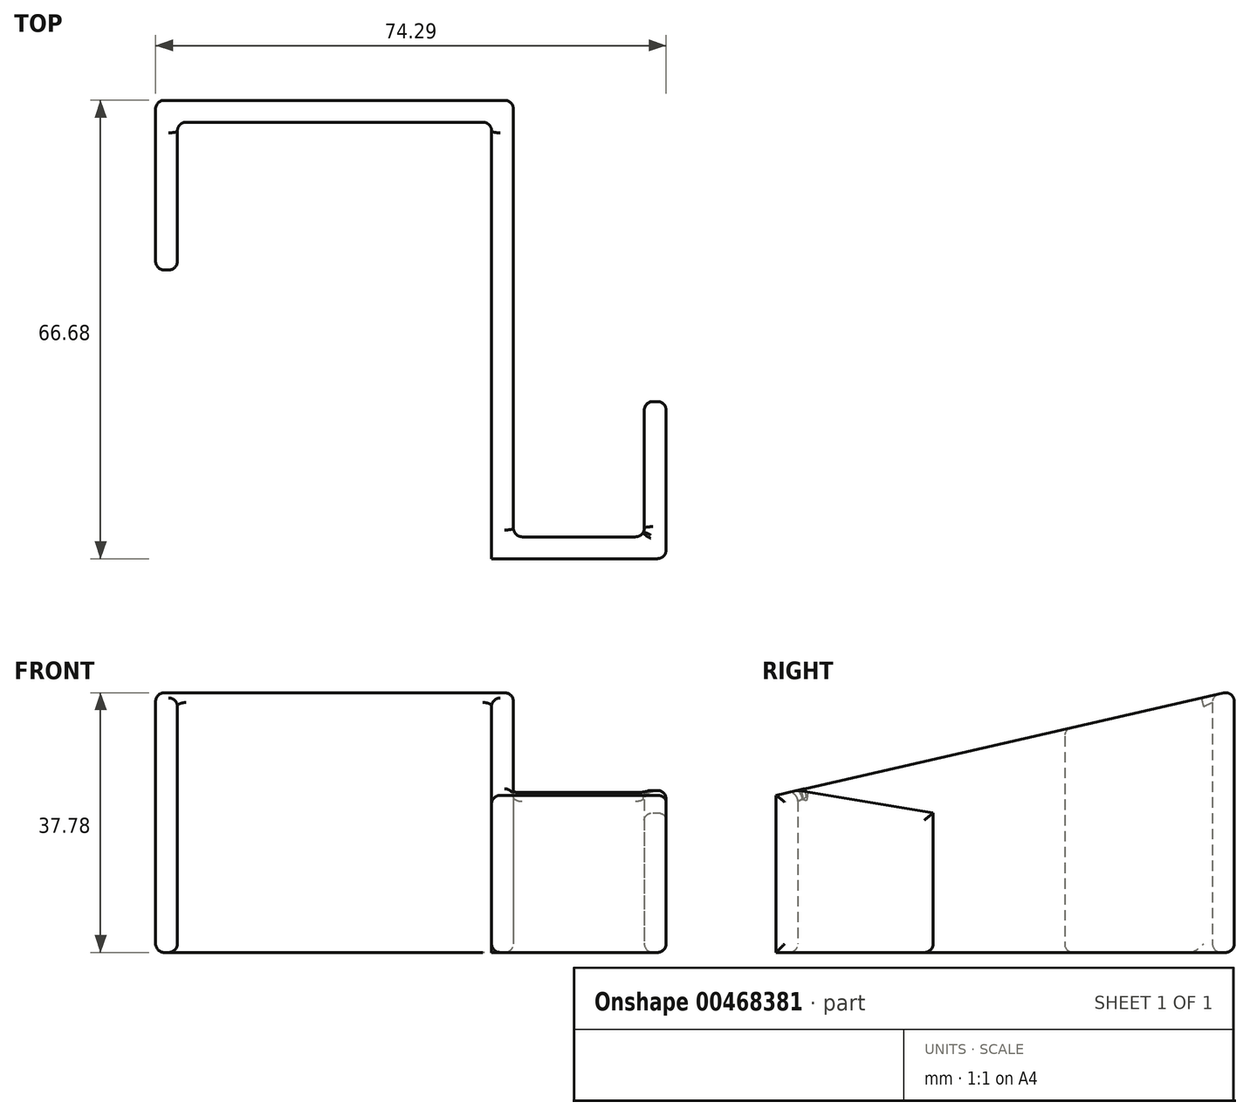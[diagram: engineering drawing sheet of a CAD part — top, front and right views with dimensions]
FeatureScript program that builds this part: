
annotation { "Feature Type Name" : "Feature", "Feature Type Description" : "" }
export const myFeature = defineFeature(function(context is Context, id is Id, definition is map)
    precondition{}
    {
        {
            var Q0;
            Q0=qCreatedBy(makeId("Top.planeOp"),FACE);
            var sketch = newSketch(context, id + "F0", { "sketchPlane" : qUnion([Q0])});
            skLineSegment(sketch, "E0", {"start": v(-23.13, 0) * mm, "end": v(-23.13, 21.5) * mm});
            skLineSegment(sketch, "E1", {"start": v(-23.13, 21.5) * mm, "end": v(22.6, 21.5) * mm});
            skLineSegment(sketch, "E2", {"start": v(22.6, 21.5) * mm, "end": v(22.6, -42) * mm});
            skLineSegment(sketch, "E3", {"start": v(22.6, -42) * mm, "end": v(48, -42) * mm});
            skLineSegment(sketch, "E4", {"start": v(48, -42) * mm, "end": v(48, -19.14) * mm});
            skLineSegment(sketch, "E5", {"start": v(48, -19.14) * mm, "end": v(44.82, -19.14) * mm});
            skLineSegment(sketch, "E6", {"start": v(44.82, -19.14) * mm, "end": v(44.82, -38.82) * mm});
            skLineSegment(sketch, "E7", {"start": v(44.82, -38.82) * mm, "end": v(25.77, -38.82) * mm});
            skLineSegment(sketch, "E8", {"start": v(25.77, -38.82) * mm, "end": v(25.77, 24.68) * mm});
            skLineSegment(sketch, "E9", {"start": v(25.77, 24.68) * mm, "end": v(-26.3, 24.68) * mm});
            skLineSegment(sketch, "E10", {"start": v(-26.3, 24.68) * mm, "end": v(-26.3, 0) * mm});
            skLineSegment(sketch, "E11", {"start": v(-26.3, 0) * mm, "end": v(-23.13, 0) * mm});
            skSolve(sketch);
        }
        {
            var Q0;
            Q0=makeQuery(id+"F0.imprint","IMPRINT",FACE,{"disambiguationData":[TD([[makeQuery(id+"F0.imprint","IMPRINT",EDGE,{"derivedFrom":sQuery(id+"F0.wireOp",EDGE,"E0")}),1.0]])]});
            extrude(context, id + "F1", {"entities" : qUnion([Q0]), "depth" : 38.1 * mm});
        }
        {
            var Q0;
            Q0=qCreatedBy(makeId("Right.planeOp"),FACE);
            var sketch = newSketch(context, id + "F2", { "sketchPlane" : qUnion([Q0])});
            skPoint(sketch, "E12.0", {"position": v(24.68, 38.1) * mm});
            skLineSegment(sketch, "E13", {"start": v(-42, 22.86) * mm, "end": v(24.68, 38.1) * mm});
            skLineSegment(sketch, "E14", {"start": v(-20.6, 65.52) * mm, "end": v(24.68, 38.1) * mm});
            skLineSegment(sketch, "E15", {"start": v(-20.6, 65.52) * mm, "end": v(-63.7, 38.1) * mm});
            skLineSegment(sketch, "E16", {"start": v(-63.7, 38.1) * mm, "end": v(-42, 22.86) * mm});
            skPoint(sketch, "E17.0.0.end.orphan", {"position": v(-19.14, 0) * mm});
            skPoint(sketch, "E17.0.1.end.orphan", {"position": v(-19.14, 38.1) * mm});
            skPoint(sketch, "E18.orphan", {"position": v(-42, 0) * mm});
            skPoint(sketch, "E19.0.start.orphan", {"position": v(-42, 38.1) * mm});
            skSolve(sketch);
        }
        {
            var Q0;
            Q0=makeQuery(id+"F2.imprint","IMPRINT",FACE,{"disambiguationData":[TD([[makeQuery(id+"F2.imprint","IMPRINT",EDGE,{"derivedFrom":sQuery(id+"F2.wireOp",EDGE,"E13")}),1.0]])]});
            extrude(context, id + "F3", {"entities" : qUnion([Q0]), "operationType" : NewBodyOperationType.REMOVE, "endBound" : BoundingType.SYMMETRIC, "oppositeDirection" : true, "depth" : 127 * mm});
        }
        {
            var Q0;
            Q0=makeQuery(id+"F1.opExtrude","SWEPT_FACE",FACE,{"disambiguationData":[OSD([sQuery(id+"F0.wireOp",EDGE,"E4")])]});
            var sketch = newSketch(context, id + "F4", { "sketchPlane" : qUnion([Q0])});
            skPoint(sketch, "E20.0.1.start.orphan", {"position": v(-19.14, 28.09) * mm});
            skLineSegment(sketch, "E21.0", {"start": v(-38.82, 23.59) * mm, "end": v(-19.14, 28.09) * mm});
            skLineSegment(sketch, "E22", {"start": v(-38.82, 23.59) * mm, "end": v(-19.14, 20.32) * mm});
            skPoint(sketch, "E23.orphan", {"position": v(-42, 0) * mm});
            skPoint(sketch, "E24.end.orphan", {"position": v(-19.14, 5.08) * mm});
            skPoint(sketch, "E20.0.3.end.orphan", {"position": v(-19.14, 0) * mm});
            skPoint(sketch, "E20.0.3.start.orphan", {"position": v(-38.82, 0) * mm});
            skLineSegment(sketch, "E25", {"start": v(-19.14, 20.32) * mm, "end": v(-19.14, 28.09) * mm});
            skSolve(sketch);
        }
        {
            var Q0;
            Q0=makeQuery(id+"F4.imprint","IMPRINT",FACE,{"disambiguationData":[TD([[makeQuery(id+"F4.imprint","IMPRINT",EDGE,{"derivedFrom":sQuery(id+"F4.wireOp",EDGE,"E21.0")}),1.0]])]});
            extrude(context, id + "F5", {"entities" : qUnion([Q0]), "operationType" : NewBodyOperationType.REMOVE, "oppositeDirection" : true, "depth" : 6.35 * mm});
        }
        {
            var Q0;
            Q0=makeQuery(id+"F1.opExtrude","SWEPT_FACE",FACE,{"disambiguationData":[OSD([sQuery(id+"F0.wireOp",EDGE,"E0")])]});
            var Q1;
            Q1=makeQuery(id+"F1.opExtrude","SWEPT_FACE",FACE,{"disambiguationData":[OSD([sQuery(id+"F0.wireOp",EDGE,"E8")])]});
            var Q2;
            Q2=makeQuery(id+"F1.opExtrude","SWEPT_FACE",FACE,{"disambiguationData":[OSD([sQuery(id+"F0.wireOp",EDGE,"E4")])]});
            var Q3;
            Q3=makeQuery(id+"F3.boolean.opBoolean","INTERSECT",EDGE,{"derivedFrom":[makeQuery(id+"F1.opExtrude","SWEPT_FACE",FACE,{"disambiguationData":[OSD([sQuery(id+"F0.wireOp",EDGE,"E7")])]}),makeQuery(id+"F3.opExtrude","SWEPT_FACE",FACE,{"disambiguationData":[OSD([sQuery(id+"F2.wireOp",EDGE,"E13")])]})]});
            var Q4;
            Q4=makeQuery(id+"F1.opExtrude","CAP_EDGE",EDGE,{"disambiguationData":[OSD([sQuery(id+"F0.wireOp",EDGE,"E1")])],"isStart":true});
            var Q5;
            Q5=makeQuery(id+"F1.opExtrude","SWEPT_EDGE",EDGE,{"disambiguationData":[OSD([sQuery(id+"F0.wireOp",EDGE,"E0"),sQuery(id+"F0.wireOp",EDGE,"E11")])]});
            var Q6;
            Q6=makeQuery(id+"F1.opExtrude","CAP_EDGE",EDGE,{"disambiguationData":[OSD([sQuery(id+"F0.wireOp",EDGE,"E7")])],"isStart":true});
            var Q7;
            Q7=makeQuery(id+"F1.opExtrude","SWEPT_EDGE",EDGE,{"disambiguationData":[OSD([sQuery(id+"F0.wireOp",EDGE,"E7"),sQuery(id+"F0.wireOp",EDGE,"E8")])]});
            var Q8;
            Q8=makeQuery(id+"F1.opExtrude","SWEPT_EDGE",EDGE,{"disambiguationData":[OSD([sQuery(id+"F0.wireOp",EDGE,"E0"),sQuery(id+"F0.wireOp",EDGE,"E1")])]});
            var Q9;
            Q9=makeQuery(id+"F1.opExtrude","SWEPT_EDGE",EDGE,{"disambiguationData":[OSD([sQuery(id+"F0.wireOp",EDGE,"E8"),sQuery(id+"F0.wireOp",EDGE,"E9")])]});
            var Q10;
            Q10=makeQuery(id+"F3.boolean.opBoolean","MERGE",EDGE,{"derivedFrom":[makeQuery(id+"F1.opExtrude","CAP_EDGE",EDGE,{"disambiguationData":[OSD([sQuery(id+"F0.wireOp",EDGE,"E9")])],"isStart":false}),makeQuery(id+"F3.opExtrude","SWEPT_EDGE",EDGE,{"disambiguationData":[OSD([sQuery(id+"F2.wireOp",EDGE,"E13"),sQuery(id+"F2.wireOp",EDGE,"E14")])]})]});
            var Q11;
            Q11=makeQuery(id+"F3.boolean.opBoolean","INTERSECT",EDGE,{"derivedFrom":[makeQuery(id+"F1.opExtrude","SWEPT_FACE",FACE,{"disambiguationData":[OSD([sQuery(id+"F0.wireOp",EDGE,"E1")])]}),makeQuery(id+"F3.opExtrude","SWEPT_FACE",FACE,{"disambiguationData":[OSD([sQuery(id+"F2.wireOp",EDGE,"E13")])]})]});
            var Q12;
            Q12=makeQuery(id+"F1.opExtrude","CAP_EDGE",EDGE,{"disambiguationData":[OSD([sQuery(id+"F0.wireOp",EDGE,"E0")])],"isStart":true});
            var Q13;
            Q13=makeQuery(id+"F1.opExtrude","SWEPT_EDGE",EDGE,{"disambiguationData":[OSD([sQuery(id+"F0.wireOp",EDGE,"E10"),sQuery(id+"F0.wireOp",EDGE,"E11")])]});
            var Q14;
            Q14=makeQuery(id+"F3.boolean.opBoolean","INTERSECT",EDGE,{"derivedFrom":[makeQuery(id+"F1.opExtrude","SWEPT_FACE",FACE,{"disambiguationData":[OSD([sQuery(id+"F0.wireOp",EDGE,"E10")])]}),makeQuery(id+"F3.opExtrude","SWEPT_FACE",FACE,{"disambiguationData":[OSD([sQuery(id+"F2.wireOp",EDGE,"E13")])]})]});
            var Q15;
            Q15=makeQuery(id+"F3.boolean.opBoolean","INTERSECT",EDGE,{"derivedFrom":[makeQuery(id+"F1.opExtrude","SWEPT_FACE",FACE,{"disambiguationData":[OSD([sQuery(id+"F0.wireOp",EDGE,"E0")])]}),makeQuery(id+"F3.opExtrude","SWEPT_FACE",FACE,{"disambiguationData":[OSD([sQuery(id+"F2.wireOp",EDGE,"E13")])]})]});
            var Q16;
            Q16=makeQuery(id+"F3.boolean.opBoolean","COPY",EDGE,{"derivedFrom":makeQuery(id+"F3.opExtrude","SWEPT_EDGE",EDGE,{"disambiguationData":[OSD([sQuery(id+"F2.wireOp",EDGE,"E13"),sQuery(id+"F2.wireOp",EDGE,"E16")])]})});
            var Q17;
            Q17=makeQuery(id+"F3.boolean.opBoolean","INTERSECT",EDGE,{"derivedFrom":[makeQuery(id+"F1.opExtrude","SWEPT_FACE",FACE,{"disambiguationData":[OSD([sQuery(id+"F0.wireOp",EDGE,"E8")])]}),makeQuery(id+"F3.opExtrude","SWEPT_FACE",FACE,{"disambiguationData":[OSD([sQuery(id+"F2.wireOp",EDGE,"E13")])]})]});
            var Q18;
            Q18=makeQuery(id+"F3.boolean.opBoolean","INTERSECT",EDGE,{"derivedFrom":[makeQuery(id+"F1.opExtrude","SWEPT_FACE",FACE,{"disambiguationData":[OSD([sQuery(id+"F0.wireOp",EDGE,"E2")])]}),makeQuery(id+"F3.opExtrude","SWEPT_FACE",FACE,{"disambiguationData":[OSD([sQuery(id+"F2.wireOp",EDGE,"E13")])]})]});
            var Q19;
            Q19=makeQuery(id+"F1.opExtrude","CAP_EDGE",EDGE,{"disambiguationData":[OSD([sQuery(id+"F0.wireOp",EDGE,"E8")])],"isStart":true});
            var Q20;
            Q20=makeQuery(id+"F5.boolean.opBoolean","INTERSECT",EDGE,{"derivedFrom":[makeQuery(id+"F1.opExtrude","SWEPT_FACE",FACE,{"disambiguationData":[OSD([sQuery(id+"F0.wireOp",EDGE,"E6")])]}),makeQuery(id+"F5.opExtrude","SWEPT_FACE",FACE,{"disambiguationData":[OSD([sQuery(id+"F4.wireOp",EDGE,"E22")])]})]});
            var Q21;
            Q21=makeQuery(id+"F1.opExtrude","CAP_EDGE",EDGE,{"disambiguationData":[OSD([sQuery(id+"F0.wireOp",EDGE,"E4")])],"isStart":true});
            var Q22;
            Q22=makeQuery(id+"F5.boolean.opBoolean","COPY",EDGE,{"derivedFrom":makeQuery(id+"F5.opExtrude","CAP_EDGE",EDGE,{"disambiguationData":[OSD([sQuery(id+"F4.wireOp",EDGE,"E22")])],"isStart":true})});
            var Q23;
            Q23=makeQuery(id+"F1.opExtrude","SWEPT_EDGE",EDGE,{"disambiguationData":[OSD([sQuery(id+"F0.wireOp",EDGE,"E6"),sQuery(id+"F0.wireOp",EDGE,"E7")])]});
            var Q24;
            Q24=makeQuery(id+"F1.opExtrude","CAP_EDGE",EDGE,{"disambiguationData":[OSD([sQuery(id+"F0.wireOp",EDGE,"E5")])],"isStart":true});
            var Q25;
            Q25=makeQuery(id+"F1.opExtrude","SWEPT_EDGE",EDGE,{"disambiguationData":[OSD([sQuery(id+"F0.wireOp",EDGE,"E3"),sQuery(id+"F0.wireOp",EDGE,"E4")])]});
            var Q26;
            Q26=makeQuery(id+"F1.opExtrude","SWEPT_EDGE",EDGE,{"disambiguationData":[OSD([sQuery(id+"F0.wireOp",EDGE,"E1"),sQuery(id+"F0.wireOp",EDGE,"E2")])]});
            var Q27;
            Q27=makeQuery(id+"F1.opExtrude","SWEPT_EDGE",EDGE,{"disambiguationData":[OSD([sQuery(id+"F0.wireOp",EDGE,"E9"),sQuery(id+"F0.wireOp",EDGE,"E10")])]});
            var Q28;
            Q28=makeQuery(id+"F1.opExtrude","CAP_EDGE",EDGE,{"disambiguationData":[OSD([sQuery(id+"F0.wireOp",EDGE,"E9")])],"isStart":true});
            var Q29;
            Q29=makeQuery(id+"F1.opExtrude","CAP_EDGE",EDGE,{"disambiguationData":[OSD([sQuery(id+"F0.wireOp",EDGE,"E10")])],"isStart":true});
            var Q30;
            Q30=makeQuery(id+"F1.opExtrude","CAP_EDGE",EDGE,{"disambiguationData":[OSD([sQuery(id+"F0.wireOp",EDGE,"E11")])],"isStart":true});
            var Q31;
            Q31=makeQuery(id+"F1.opExtrude","SWEPT_EDGE",EDGE,{"disambiguationData":[OSD([sQuery(id+"F0.wireOp",EDGE,"E5"),sQuery(id+"F0.wireOp",EDGE,"E6")])]});
            var Q32;
            Q32=makeQuery(id+"F1.opExtrude","SWEPT_EDGE",EDGE,{"disambiguationData":[OSD([sQuery(id+"F0.wireOp",EDGE,"E4"),sQuery(id+"F0.wireOp",EDGE,"E5")])]});
            var Q33;
            Q33=makeQuery(id+"F1.opExtrude","CAP_EDGE",EDGE,{"disambiguationData":[OSD([sQuery(id+"F0.wireOp",EDGE,"E6")])],"isStart":true});
            var Q34;
            Q34=makeQuery(id+"F5.boolean.opBoolean","COPY",EDGE,{"derivedFrom":makeQuery(id+"F5.opExtrude","SWEPT_EDGE",EDGE,{"disambiguationData":[OSD([sQuery(id+"F0.wireOp",EDGE,"E4"),sQuery(id+"F0.wireOp",EDGE,"E5"),sQuery(id+"F4.wireOp",EDGE,"E22"),sQuery(id+"F4.wireOp",EDGE,"E25")])]})});
            var Q35;
            Q35=makeQuery(id+"F3.boolean.opBoolean","INTERSECT",EDGE,{"derivedFrom":[makeQuery(id+"F1.opExtrude","SWEPT_FACE",FACE,{"disambiguationData":[OSD([sQuery(id+"F0.wireOp",EDGE,"E11")])]}),makeQuery(id+"F3.opExtrude","SWEPT_FACE",FACE,{"disambiguationData":[OSD([sQuery(id+"F2.wireOp",EDGE,"E13")])]})]});
            var Q36;
            Q36=makeQuery(id+"F5.boolean.opBoolean","COPY",EDGE,{"derivedFrom":makeQuery(id+"F5.opExtrude","SWEPT_EDGE",EDGE,{"disambiguationData":[OSD([sQuery(id+"F0.wireOp",EDGE,"E4"),sQuery(id+"F2.wireOp",EDGE,"E13"),sQuery(id+"F4.wireOp",EDGE,"E21.0"),sQuery(id+"F4.wireOp",EDGE,"E22")])]})});
            var Q37;
            Q37=makeQuery(id+"F3.boolean.opBoolean","INTERSECT",EDGE,{"derivedFrom":[makeQuery(id+"F1.opExtrude","SWEPT_FACE",FACE,{"disambiguationData":[OSD([sQuery(id+"F0.wireOp",EDGE,"E4")])]}),makeQuery(id+"F3.opExtrude","SWEPT_FACE",FACE,{"disambiguationData":[OSD([sQuery(id+"F2.wireOp",EDGE,"E13")])]})]});
            fillet(context, id + "F6", {"entities" : qUnion([Q0, Q1, Q2, Q3, Q4, Q5, Q6, Q7, Q8, Q9, Q10, Q11, Q12, Q13, Q14, Q15, Q16, Q17, Q18, Q19, Q20, Q21, Q22, Q23, Q24, Q25, Q26, Q27, Q28, Q29, Q30, Q31, Q32, Q33, Q34, Q35, Q36, Q37]), "radius" : 1.27 * mm, "tangentPropagation" : true, "allowEdgeOverflow" : false});
        }
    });
